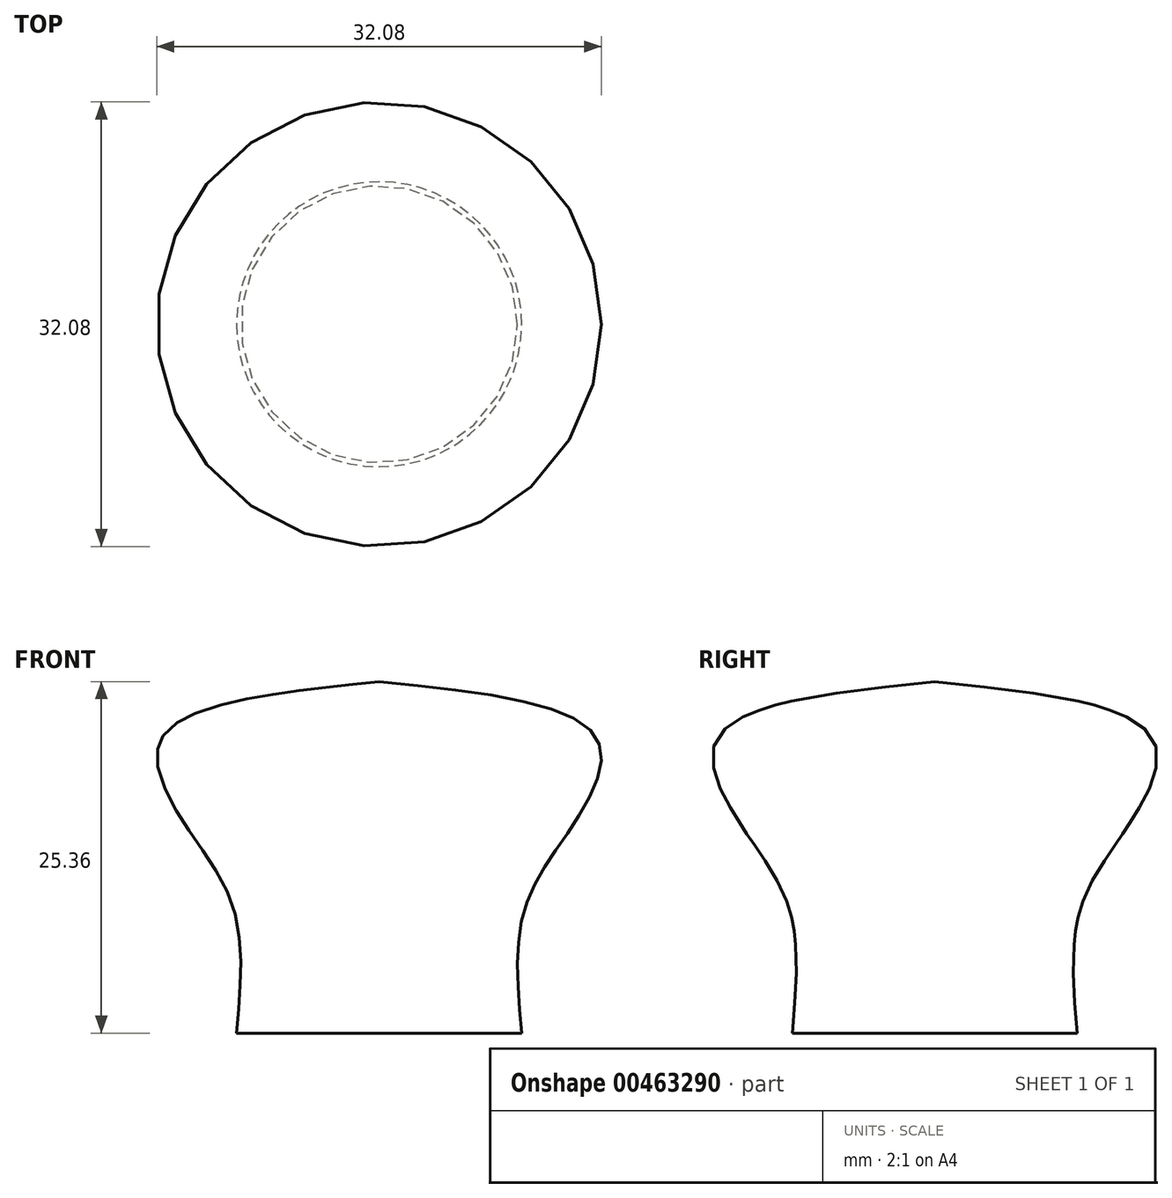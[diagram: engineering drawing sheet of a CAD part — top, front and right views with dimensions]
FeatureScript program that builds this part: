
annotation { "Feature Type Name" : "Feature", "Feature Type Description" : "" }
export const myFeature = defineFeature(function(context is Context, id is Id, definition is map)
    precondition{}
    {
        {
            var Q0;
            Q0=qCreatedBy(makeId("Front.planeOp"),FACE);
            var sketch = newSketch(context, id + "F0", { "sketchPlane" : qUnion([Q0])});
            skFitSpline(sketch, "E0", {"points": [v(10.28, 0) * mm, v(10.49, 8.96) * mm, v(14.23, 15.4) * mm, v(15.68, 21.31) * mm, v(0, 25.36) * mm], "startDerivative": vector(-3.53, 39) * mm, "endDerivative": vector(-64.33, 6.57) * mm});
            skLineSegment(sketch, "E1", {"start": v(10.28, 0) * mm, "end": v(0, 0) * mm});
            skLineSegment(sketch, "E2", {"start": v(0, 28.48) * mm, "end": v(0, -10.56) * mm, "construction": true});
            skSolve(sketch);
        }
        {
            var Q0;
            Q0=sQuery(id+"F0.wireOp",EDGE,"E0");
            var Q1;
            Q1=sQuery(id+"F0.wireOp",EDGE,"E1");
            var Q2;
            Q2=sQuery(id+"F0.wireOp",EDGE,"E2");
            revolve(context, id + "F1", {"bodyType" : ToolBodyType.SURFACE, "surfaceEntities" : qUnion([Q0, Q1]), "axis" : qUnion([Q2]), "revolveType" : RevolveType.FULL});
        }
    });
